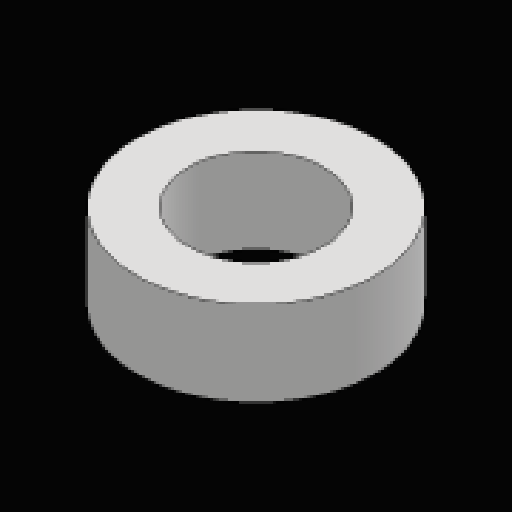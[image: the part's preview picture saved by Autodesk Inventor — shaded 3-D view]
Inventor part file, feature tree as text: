
AUTODESK INVENTOR PART (.ipt)
format: ipt  version: 2023.2 (Build 272271030, 271C)  size: 90,624 bytes
history: native  units: mm
features: revolve x1, sketch x1
ambient origin geometry x8: Origin, YZ Plane, XZ Plane, XY Plane, X Axis, Y Axis, Z Axis, Center Point
bodies: Solid1 (feature_tree)
feature tree (2):
  revolve  "Revolution1"  [1 undecoded]
  sketch  "Sketch1"  dims[d0=2.0mm d1=2.5mm d2=3.5mm d3=90.0deg]
note: 1 required parameter value undecoded (feature->parameter linkage not recoverable at this tier; creation-order binding heuristic only, values carry confidence <= 0.55)
